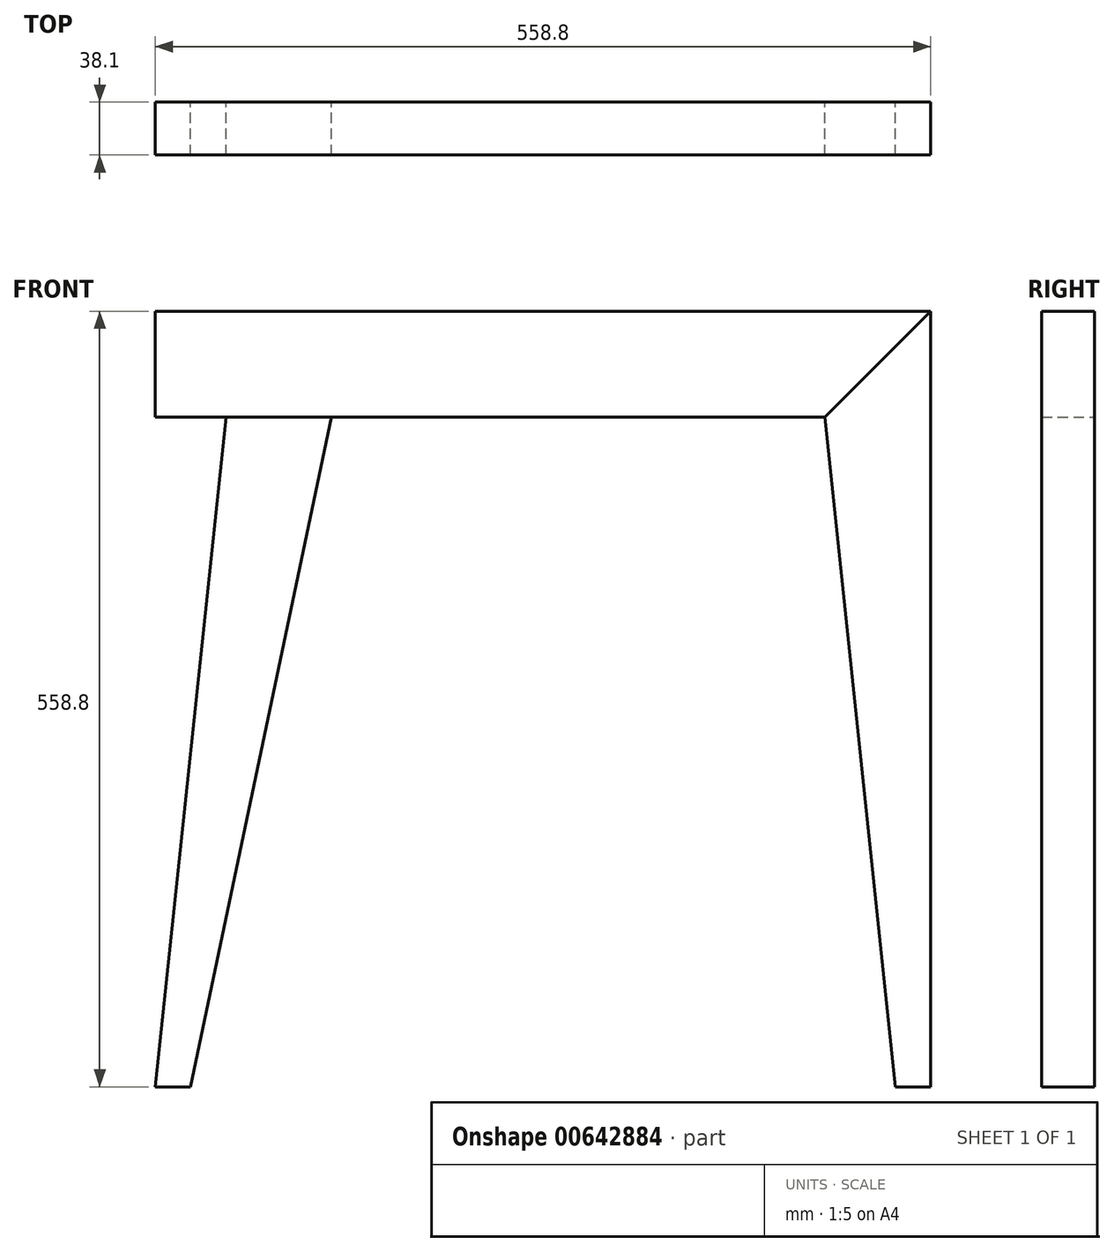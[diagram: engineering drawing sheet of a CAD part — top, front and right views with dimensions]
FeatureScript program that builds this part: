
annotation { "Feature Type Name" : "Feature", "Feature Type Description" : "" }
export const myFeature = defineFeature(function(context is Context, id is Id, definition is map)
    precondition{}
    {
        {
            var Q0;
            Q0=qCreatedBy(makeId("Front.planeOp"),FACE);
            var sketch = newSketch(context, id + "F0", { "sketchPlane" : qUnion([Q0])});
            skLineSegment(sketch, "E0.bottom", {"start": v(215.9, -38.1) * mm, "end": v(-266.7, -38.1) * mm});
            skLineSegment(sketch, "E0.top", {"start": v(292.1, 38.1) * mm, "end": v(-266.7, 38.1) * mm});
            skLineSegment(sketch, "E0.left", {"start": v(292.1, -38.1) * mm, "end": v(292.1, 38.1) * mm});
            skLineSegment(sketch, "E0.right", {"start": v(-266.7, -38.1) * mm, "end": v(-266.7, 38.1) * mm});
            skPoint(sketch, "E0.middle", {"position": v(12.7, 0) * mm});
            skLineSegment(sketch, "E1", {"start": v(-215.62, -38.1) * mm, "end": v(-266.7, -520.7) * mm});
            skLineSegment(sketch, "E2", {"start": v(-266.7, -520.7) * mm, "end": v(-241.3, -520.7) * mm});
            skLineSegment(sketch, "E3", {"start": v(-241.3, -520.7) * mm, "end": v(-139.7, -38.1) * mm});
            skLineSegment(sketch, "E4", {"start": v(292.1, 38.1) * mm, "end": v(215.9, -38.1) * mm});
            skLineSegment(sketch, "E5", {"start": v(292.1, -38.1) * mm, "end": v(292.1, -520.7) * mm});
            skLineSegment(sketch, "E6", {"start": v(215.9, -38.1) * mm, "end": v(266.7, -520.7) * mm});
            skLineSegment(sketch, "E7", {"start": v(266.7, -520.7) * mm, "end": v(292.1, -520.7) * mm});
            skSolve(sketch);
        }
        {
            var Q0;
            Q0=makeQuery(id+"F0.imprint","IMPRINT",FACE,{"disambiguationData":[TD([[makeQuery(id+"F0.imprint","IMPRINT",EDGE,{"derivedFrom":sQuery(id+"F0.wireOp",EDGE,"E0.top")}),1.0]])]});
            extrude(context, id + "F1", {"entities" : qUnion([Q0]), "depth" : 38.1 * mm, "offsetDistance" : 25.4 * mm});
        }
        {
            var Q0;
            {var subQ0=sQuery(id+"F0.wireOp",EDGE,"E1");Q0=makeQuery(id+"F0.imprint","IMPRINT",FACE,{"disambiguationData":[TD([[makeQuery(id+"F0.imprint","IMPRINT",EDGE,{"derivedFrom":subQ0}),1.0]])]});}
            var Q1;
            Q1=makeQuery(id+"F0.imprint","IMPRINT",FACE,{"disambiguationData":[TD([[makeQuery(id+"F0.imprint","IMPRINT",EDGE,{"derivedFrom":sQuery(id+"F0.wireOp",EDGE,"E0.left")}),1.0]])]});
            extrude(context, id + "F2", {"entities" : qUnion([Q0, Q1]), "depth" : 38.1 * mm, "offsetDistance" : 25.4 * mm});
        }
    });
